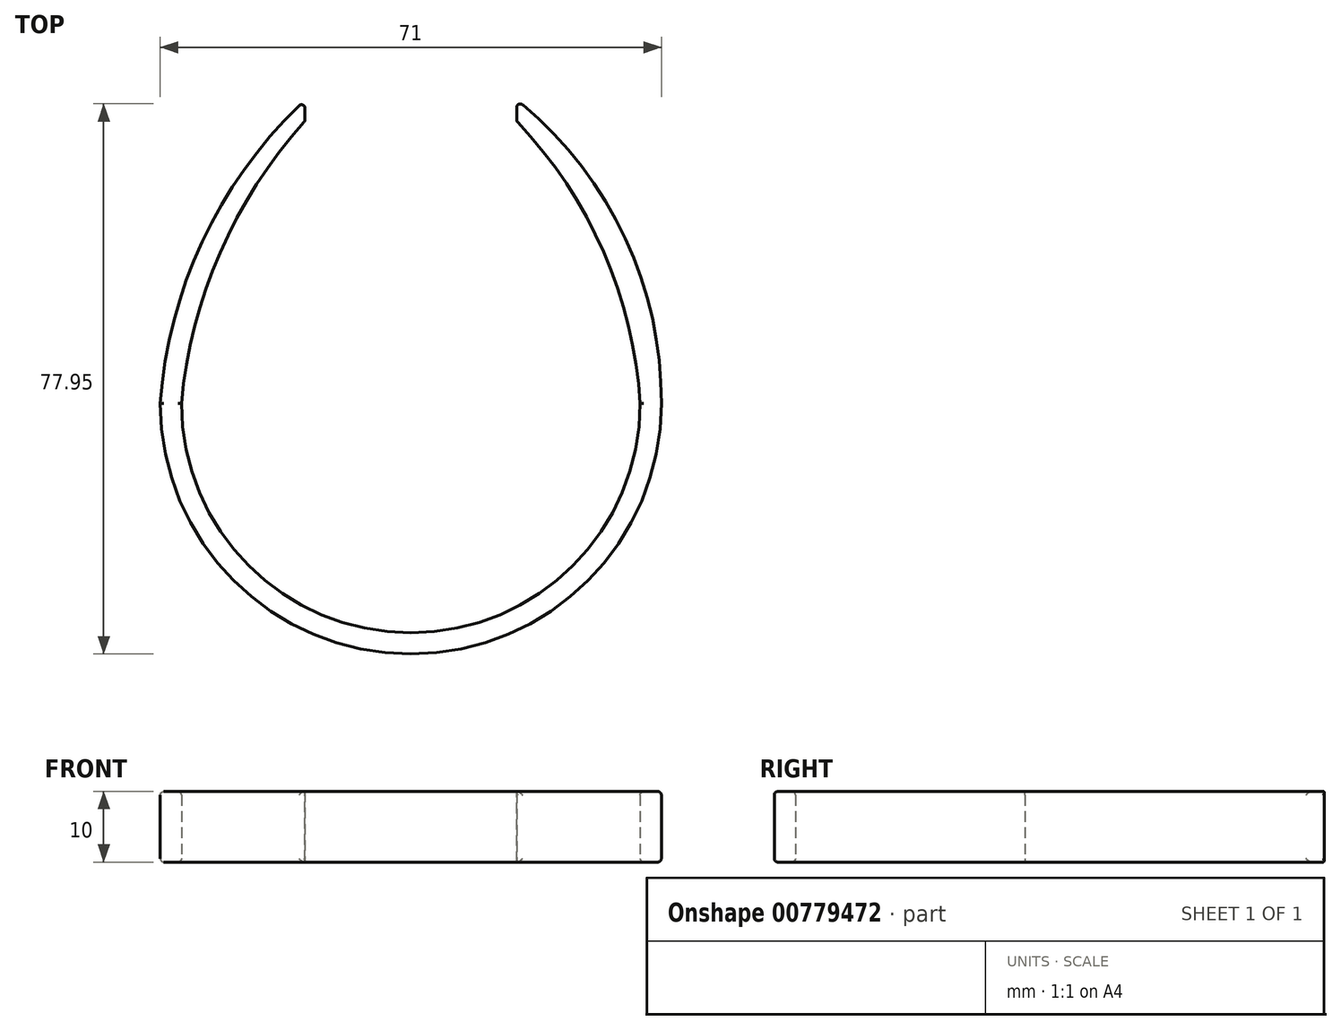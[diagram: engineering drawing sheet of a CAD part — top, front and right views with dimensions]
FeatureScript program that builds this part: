
annotation { "Feature Type Name" : "Feature", "Feature Type Description" : "" }
export const myFeature = defineFeature(function(context is Context, id is Id, definition is map)
    precondition{}
    {
        {
            var Q0;
            Q0=qCreatedBy(makeId("Top.planeOp"),FACE);
            var sketch = newSketch(context, id + "F0", { "sketchPlane" : qUnion([Q0])});
            skArc(sketch, "E0", {"start": v(-32.5, 0) * mm, "mid": v(0, -32.5) * mm, "end": v(32.5, 0) * mm});
            skArc(sketch, "E1.0", {"start": v(-35.5, 0) * mm, "mid": v(0, -35.5) * mm, "end": v(35.5, 0) * mm});
            skArc(sketch, "E2", {"start": v(-15, 43) * mm, "mid": v(-29.3, 23.43) * mm, "end": v(-35.5, 0) * mm});
            skArc(sketch, "E3", {"start": v(35.5, 0) * mm, "mid": v(30.19, 23.85) * mm, "end": v(15, 43) * mm});
            skArc(sketch, "E4", {"start": v(32.5, 0) * mm, "mid": v(27.28, 21.54) * mm, "end": v(15, 40) * mm});
            skArc(sketch, "E5", {"start": v(-15, 40) * mm, "mid": v(-27, 21.42) * mm, "end": v(-32.5, 0) * mm});
            skPoint(sketch, "E6.orphan", {"position": v(0, 43) * mm});
            skLineSegment(sketch, "E7.trimOffspring", {"start": v(-15, 40) * mm, "end": v(-15, 43) * mm});
            skLineSegment(sketch, "E8.trimOffspring", {"start": v(15, 40) * mm, "end": v(15, 43) * mm});
            skSolve(sketch);
        }
        {
            var Q0;
            Q0=makeQuery(id+"F0.imprint","IMPRINT",FACE,{"disambiguationData":[TD([[makeQuery(id+"F0.imprint","IMPRINT",EDGE,{"derivedFrom":sQuery(id+"F0.wireOp",EDGE,"E0")}),-1.0]])]});
            extrude(context, id + "F1", {"entities" : qUnion([Q0]), "depth" : 10 * mm, "offsetDistance" : 25 * mm});
        }
        {
            var Q0;
            Q0=makeQuery(id+"F1.opExtrude","SWEPT_EDGE",EDGE,{"disambiguationData":[OSD([sQuery(id+"F0.wireOp",EDGE,"E2"),sQuery(id+"F0.wireOp",EDGE,"E7.trimOffspring")])]});
            var Q1;
            Q1=makeQuery(id+"F1.opExtrude","SWEPT_EDGE",EDGE,{"disambiguationData":[OSD([sQuery(id+"F0.wireOp",EDGE,"E3"),sQuery(id+"F0.wireOp",EDGE,"E8.trimOffspring")])]});
            var Q2;
            Q2=makeQuery(id+"F1.opExtrude","SWEPT_EDGE",EDGE,{"disambiguationData":[OSD([sQuery(id+"F0.wireOp",EDGE,"E5"),sQuery(id+"F0.wireOp",EDGE,"E7.trimOffspring")])]});
            var Q3;
            Q3=makeQuery(id+"F1.opExtrude","SWEPT_EDGE",EDGE,{"disambiguationData":[OSD([sQuery(id+"F0.wireOp",EDGE,"E4"),sQuery(id+"F0.wireOp",EDGE,"E8.trimOffspring")])]});
            var Q4;
            Q4=makeQuery(id+"F1.opExtrude","CAP_EDGE",EDGE,{"disambiguationData":[OSD([sQuery(id+"F0.wireOp",EDGE,"E4")])],"isStart":false});
            var Q5;
            Q5=makeQuery(id+"F1.opExtrude","CAP_EDGE",EDGE,{"disambiguationData":[OSD([sQuery(id+"F0.wireOp",EDGE,"E0")])],"isStart":true});
            var Q6;
            Q6=makeQuery(id+"F1.opExtrude","CAP_EDGE",EDGE,{"disambiguationData":[OSD([sQuery(id+"F0.wireOp",EDGE,"E4")])],"isStart":true});
            var Q7;
            Q7=makeQuery(id+"F1.opExtrude","CAP_EDGE",EDGE,{"disambiguationData":[OSD([sQuery(id+"F0.wireOp",EDGE,"E0")])],"isStart":false});
            var Q8;
            Q8=makeQuery(id+"F1.opExtrude","CAP_EDGE",EDGE,{"disambiguationData":[OSD([sQuery(id+"F0.wireOp",EDGE,"E2")])],"isStart":false});
            var Q9;
            Q9=makeQuery(id+"F1.opExtrude","CAP_EDGE",EDGE,{"disambiguationData":[OSD([sQuery(id+"F0.wireOp",EDGE,"E3")])],"isStart":false});
            var Q10;
            Q10=makeQuery(id+"F1.opExtrude","CAP_EDGE",EDGE,{"disambiguationData":[OSD([sQuery(id+"F0.wireOp",EDGE,"E1.0")])],"isStart":false});
            var Q11;
            Q11=makeQuery(id+"F1.opExtrude","CAP_EDGE",EDGE,{"disambiguationData":[OSD([sQuery(id+"F0.wireOp",EDGE,"E5")])],"isStart":false});
            var Q12;
            Q12=makeQuery(id+"F1.opExtrude","CAP_EDGE",EDGE,{"disambiguationData":[OSD([sQuery(id+"F0.wireOp",EDGE,"E5")])],"isStart":true});
            var Q13;
            Q13=makeQuery(id+"F1.opExtrude","CAP_EDGE",EDGE,{"disambiguationData":[OSD([sQuery(id+"F0.wireOp",EDGE,"E1.0")])],"isStart":true});
            var Q14;
            Q14=makeQuery(id+"F1.opExtrude","CAP_EDGE",EDGE,{"disambiguationData":[OSD([sQuery(id+"F0.wireOp",EDGE,"E2")])],"isStart":true});
            fillet(context, id + "F2", {"entities" : qUnion([Q0, Q1, Q2, Q3, Q4, Q5, Q6, Q7, Q8, Q9, Q10, Q11, Q12, Q13, Q14]), "radius" : 0.5 * mm, "tangentPropagation" : true, "allowEdgeOverflow" : false});
        }
    });
